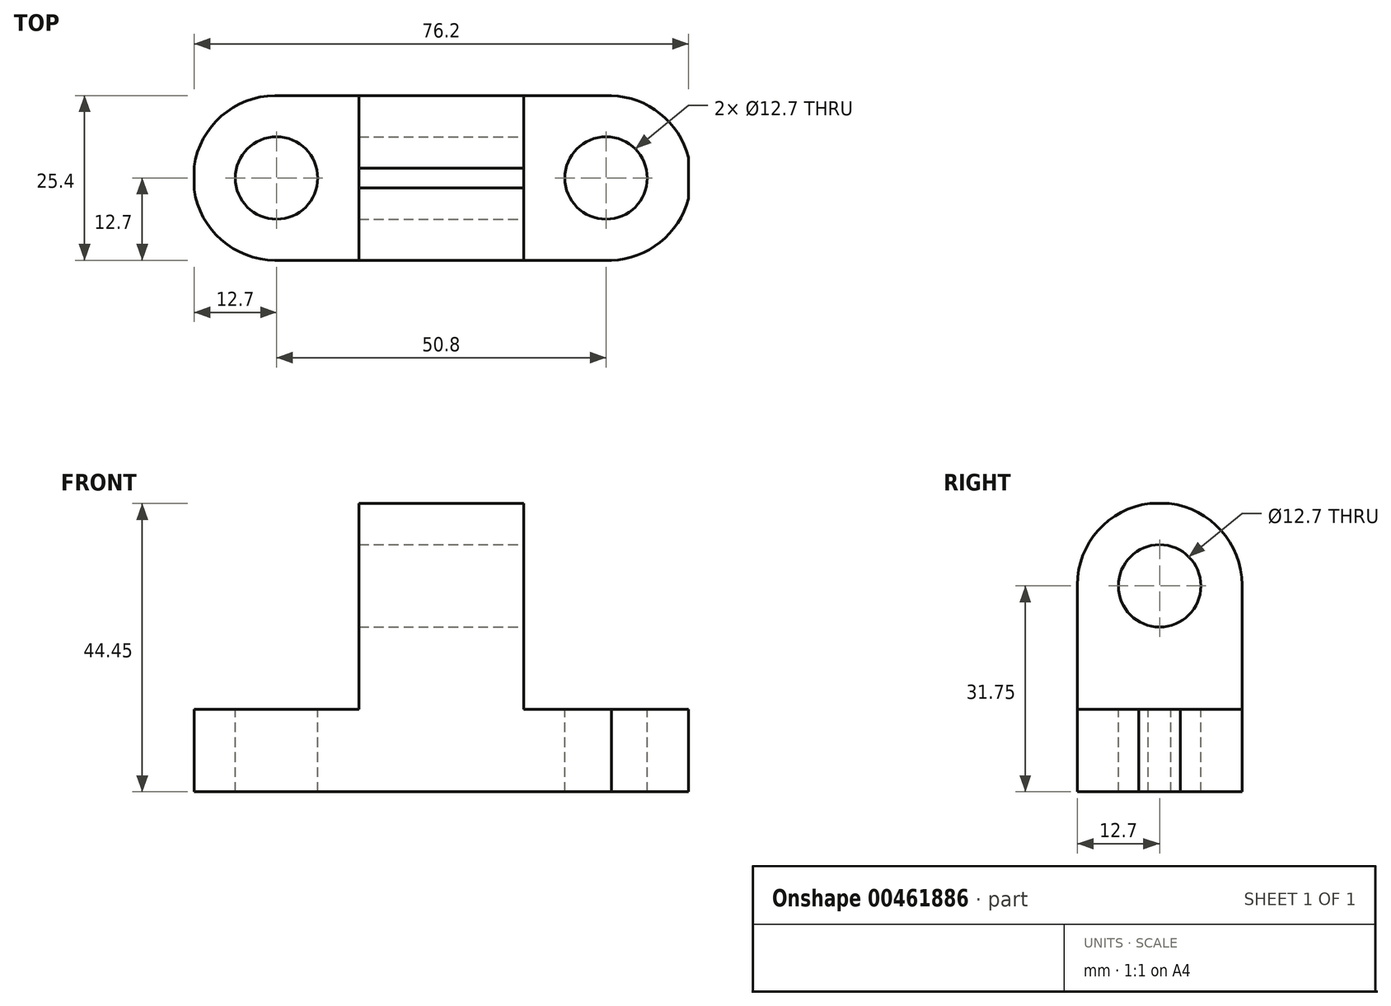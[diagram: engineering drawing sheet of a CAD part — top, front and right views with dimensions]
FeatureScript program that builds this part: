
annotation { "Feature Type Name" : "Feature", "Feature Type Description" : "" }
export const myFeature = defineFeature(function(context is Context, id is Id, definition is map)
    precondition{}
    {
        {
            var Q0;
            Q0=qCreatedBy(makeId("Front.planeOp"),FACE);
            var sketch = newSketch(context, id + "F0", { "sketchPlane" : qUnion([Q0])});
            skLineSegment(sketch, "E0", {"start": v(0, 0) * mm, "end": v(76.2, 0) * mm});
            skLineSegment(sketch, "E1", {"start": v(76.2, 0) * mm, "end": v(76.2, 12.7) * mm});
            skLineSegment(sketch, "E2", {"start": v(76.2, 12.7) * mm, "end": v(50.8, 12.7) * mm});
            skLineSegment(sketch, "E3", {"start": v(50.8, 12.7) * mm, "end": v(50.8, 44.45) * mm});
            skLineSegment(sketch, "E4", {"start": v(50.8, 44.45) * mm, "end": v(25.4, 44.45) * mm});
            skLineSegment(sketch, "E5", {"start": v(25.4, 44.45) * mm, "end": v(25.4, 12.7) * mm});
            skLineSegment(sketch, "E6", {"start": v(25.4, 12.7) * mm, "end": v(0, 12.7) * mm});
            skLineSegment(sketch, "E7", {"start": v(0, 12.7) * mm, "end": v(0, 0) * mm});
            skSolve(sketch);
        }
        {
            var Q0;
            Q0=makeQuery(id+"F0.imprint","IMPRINT",FACE,{"disambiguationData":[TD([[makeQuery(id+"F0.imprint","IMPRINT",EDGE,{"derivedFrom":sQuery(id+"F0.wireOp",EDGE,"E0")}),1.0]])]});
            extrude(context, id + "F1", {"entities" : qUnion([Q0]), "depth" : 25.4 * mm});
        }
        {
            var Q0;
            Q0=makeQuery(id+"F1.opExtrude","SWEPT_FACE",FACE,{"disambiguationData":[OSD([sQuery(id+"F0.wireOp",EDGE,"E3")])]});
            var sketch = newSketch(context, id + "F2", { "sketchPlane" : qUnion([Q0])});
            skCircle(sketch, "E8", {"center": v(-12.7, 31.75) * mm, "radius": 6.35 * mm});
            skArc(sketch, "E9", {"start": v(0, 31.75) * mm, "mid": v(-12.7, 44.54) * mm, "end": v(-25.4, 31.75) * mm});
            skSolve(sketch);
        }
        {
            var Q0;
            Q0=makeQuery(id+"F2.imprint","IMPRINT",FACE,{"disambiguationData":[TD([[makeQuery(id+"F2.imprint","IMPRINT",EDGE,{"derivedFrom":sQuery(id+"F2.wireOp",EDGE,"E8")}),1.0]])]});
            var Q1;
            {var subQ0=sQuery(id+"F2.wireOp",EDGE,"E9");var subQ1=sQuery(id+"F0.wireOp",EDGE,"E3");var subQ2=makeQuery(id+"F1.opExtrude","CAP_EDGE",EDGE,{"disambiguationData":[OSD([subQ1])],"isStart":true});var subQ3=makeQuery(id+"F2.imprint","INTERSECT",VERTEX,{"disambiguationData":[OD(1.0)],"derivedFrom":[subQ2,subQ0]});Q1=makeQuery(id+"F2.imprint","IMPRINT",FACE,{"disambiguationData":[TD([[makeQuery(id+"F2.imprint","IMPRINT",EDGE,{"disambiguationData":[TD([[subQ3,-1.0]])],"derivedFrom":subQ0}),-1.0]])]});}
            var Q2;
            {var subQ0=sQuery(id+"F2.wireOp",EDGE,"E9");var subQ1=sQuery(id+"F0.wireOp",EDGE,"E3");var subQ4=makeQuery(id+"F1.opExtrude","CAP_EDGE",EDGE,{"disambiguationData":[OSD([subQ1])],"isStart":false});var subQ5=makeQuery(id+"F2.imprint","INTERSECT",VERTEX,{"disambiguationData":[OD(1.0)],"derivedFrom":[subQ4,subQ0]});Q2=makeQuery(id+"F2.imprint","IMPRINT",FACE,{"disambiguationData":[TD([[makeQuery(id+"F2.imprint","IMPRINT",EDGE,{"disambiguationData":[TD([[subQ5,1.0]])],"derivedFrom":subQ0}),-1.0]])]});}
            extrude(context, id + "F3", {"entities" : qUnion([Q0, Q1, Q2]), "operationType" : NewBodyOperationType.REMOVE, "oppositeDirection" : true, "depth" : 25.4 * mm});
        }
        {
            var Q0;
            Q0=makeQuery(id+"F1.opExtrude","SWEPT_FACE",FACE,{"disambiguationData":[OSD([sQuery(id+"F0.wireOp",EDGE,"E2")])]});
            var sketch = newSketch(context, id + "F4", { "sketchPlane" : qUnion([Q0])});
            skCircle(sketch, "E10", {"center": v(63.5, -12.7) * mm, "radius": 6.35 * mm});
            skArc(sketch, "E11", {"start": v(63.5, -25.4) * mm, "mid": v(76.6, -12.7) * mm, "end": v(63.5, 0) * mm});
            skSolve(sketch);
        }
        {
            var Q0;
            Q0=makeQuery(id+"F4.imprint","IMPRINT",FACE,{"disambiguationData":[TD([[makeQuery(id+"F4.imprint","IMPRINT",EDGE,{"derivedFrom":sQuery(id+"F4.wireOp",EDGE,"E10")}),1.0]])]});
            var Q1;
            {var subQ0=sQuery(id+"F4.wireOp",EDGE,"E11");var subQ1=sQuery(id+"F0.wireOp",EDGE,"E2");var subQ4=makeQuery(id+"F1.opExtrude","CAP_EDGE",EDGE,{"disambiguationData":[OSD([subQ1])],"isStart":true});var subQ5=makeQuery(id+"F4.imprint","INTERSECT",VERTEX,{"disambiguationData":[OD(1.0)],"derivedFrom":[subQ4,subQ0]});Q1=makeQuery(id+"F4.imprint","IMPRINT",FACE,{"disambiguationData":[TD([[makeQuery(id+"F4.imprint","IMPRINT",EDGE,{"disambiguationData":[TD([[subQ5,1.0]])],"derivedFrom":subQ0}),-1.0]])]});}
            var Q2;
            {var subQ0=sQuery(id+"F4.wireOp",EDGE,"E11");var subQ1=sQuery(id+"F0.wireOp",EDGE,"E2");var subQ2=makeQuery(id+"F1.opExtrude","CAP_EDGE",EDGE,{"disambiguationData":[OSD([subQ1])],"isStart":false});var subQ3=makeQuery(id+"F4.imprint","INTERSECT",VERTEX,{"disambiguationData":[OD(1.0)],"derivedFrom":[subQ2,subQ0]});Q2=makeQuery(id+"F4.imprint","IMPRINT",FACE,{"disambiguationData":[TD([[makeQuery(id+"F4.imprint","IMPRINT",EDGE,{"disambiguationData":[TD([[subQ3,-1.0]])],"derivedFrom":subQ0}),-1.0]])]});}
            extrude(context, id + "F5", {"entities" : qUnion([Q0, Q1, Q2]), "operationType" : NewBodyOperationType.REMOVE, "oppositeDirection" : true, "depth" : 12.7 * mm});
        }
        {
            var Q0;
            Q0=makeQuery(id+"F1.opExtrude","SWEPT_FACE",FACE,{"disambiguationData":[OSD([sQuery(id+"F0.wireOp",EDGE,"E6")])]});
            var sketch = newSketch(context, id + "F6", { "sketchPlane" : qUnion([Q0])});
            skCircle(sketch, "E12", {"center": v(12.7, -12.7) * mm, "radius": 6.35 * mm});
            skArc(sketch, "E13", {"start": v(12.7, 0) * mm, "mid": v(-0.12, -12.7) * mm, "end": v(12.7, -25.4) * mm});
            skSolve(sketch);
        }
        {
            var Q0;
            Q0=makeQuery(id+"F6.imprint","IMPRINT",FACE,{"disambiguationData":[TD([[makeQuery(id+"F6.imprint","IMPRINT",EDGE,{"derivedFrom":sQuery(id+"F6.wireOp",EDGE,"E12")}),1.0]])]});
            var Q1;
            {var subQ0=sQuery(id+"F6.wireOp",EDGE,"E13");var subQ1=sQuery(id+"F0.wireOp",EDGE,"E6");var subQ2=makeQuery(id+"F1.opExtrude","CAP_EDGE",EDGE,{"disambiguationData":[OSD([subQ1])],"isStart":true});var subQ3=makeQuery(id+"F6.imprint","INTERSECT",VERTEX,{"disambiguationData":[OD(1.0)],"derivedFrom":[subQ2,subQ0]});Q1=makeQuery(id+"F6.imprint","IMPRINT",FACE,{"disambiguationData":[TD([[makeQuery(id+"F6.imprint","IMPRINT",EDGE,{"disambiguationData":[TD([[subQ3,-1.0]])],"derivedFrom":subQ0}),-1.0]])]});}
            var Q2;
            {var subQ0=sQuery(id+"F6.wireOp",EDGE,"E13");var subQ1=sQuery(id+"F0.wireOp",EDGE,"E6");var subQ4=makeQuery(id+"F1.opExtrude","CAP_EDGE",EDGE,{"disambiguationData":[OSD([subQ1])],"isStart":false});var subQ5=makeQuery(id+"F6.imprint","INTERSECT",VERTEX,{"disambiguationData":[OD(1.0)],"derivedFrom":[subQ4,subQ0]});Q2=makeQuery(id+"F6.imprint","IMPRINT",FACE,{"disambiguationData":[TD([[makeQuery(id+"F6.imprint","IMPRINT",EDGE,{"disambiguationData":[TD([[subQ5,1.0]])],"derivedFrom":subQ0}),-1.0]])]});}
            extrude(context, id + "F7", {"entities" : qUnion([Q0, Q1, Q2]), "operationType" : NewBodyOperationType.REMOVE, "oppositeDirection" : true, "depth" : 12.7 * mm});
        }
    });
